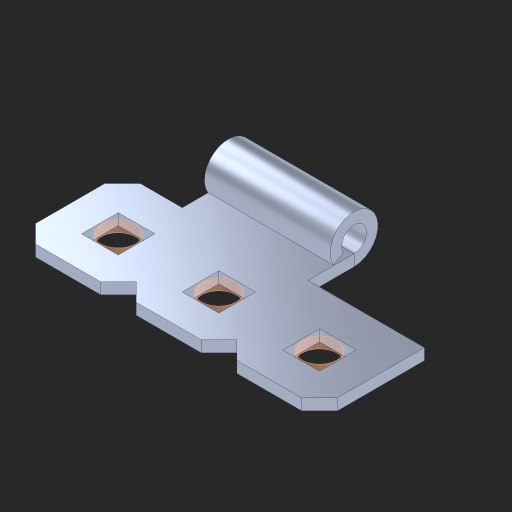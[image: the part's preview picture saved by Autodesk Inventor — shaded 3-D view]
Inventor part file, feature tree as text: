
AUTODESK INVENTOR PART (.ipt)
format: ipt  version: 2023 (Build 270158000, 158)  size: 207,360 bytes
history: native  units: in
note: dims shown in document units (in); Inventor stores cm internally (conversion verified against a paired STEP export)
features: other x5, extrude x4, sketch x2, pattern_linear x1, imported_body x1
ambient origin geometry x8: Origin, YZ Plane, XZ Plane, XY Plane, X Axis, Y Axis, Z Axis, Center Point
bodies: Body1 (feature_tree), Body2 (feature_tree), Body3 (feature_tree), Body4 (feature_tree)
feature tree (13):
  other  "Cut-Extrude3"
  other  "Bottom"
  pattern_linear  "Rectangular Pattern1"  Spacing1=1.0in  [1 undecoded]
  extrude  "Extrusion1"  Depth=1.0in
  imported_body  "Base1"
  sketch  "Sketch1"  dims[d15=0.046in d16=0.0in]
  other  "Srf1"
  other  "Srf2"
  other  "Srf3"
  sketch  "Sketch4"  dims[d19=0.5in d30=1.0in d31=0.0in d32=0.172in]
  extrude  "ExtrusionSrf1"  [1 undecoded]
  extrude  "ExtrusionSrf2"  [1 undecoded]
  extrude  "ExtrusionSrf3"  [1 undecoded]
note: 4 required parameter values undecoded (feature->parameter linkage not recoverable at this tier; creation-order binding heuristic only, values carry confidence <= 0.55)
